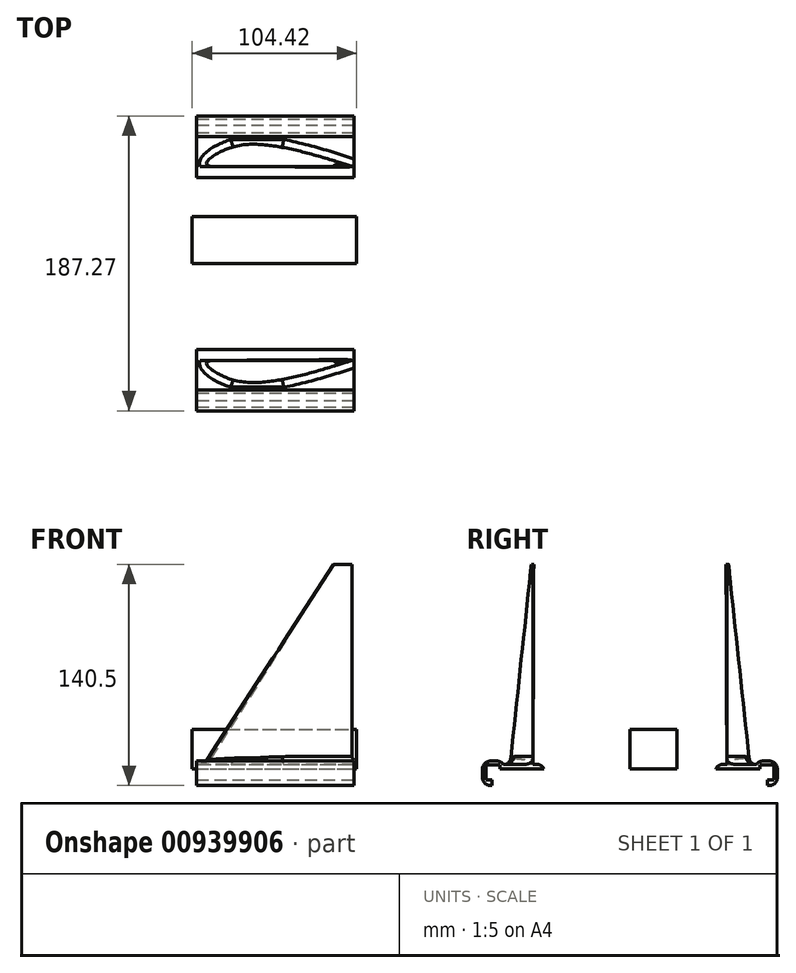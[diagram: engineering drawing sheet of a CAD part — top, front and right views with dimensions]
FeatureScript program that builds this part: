
annotation { "Feature Type Name" : "Feature", "Feature Type Description" : "" }
export const myFeature = defineFeature(function(context is Context, id is Id, definition is map)
    precondition{}
    {
        {
            var Q0;
            Q0=qCreatedBy(makeId("Top.planeOp"),FACE);
            var sketch = newSketch(context, id + "F0", { "sketchPlane" : qUnion([Q0])});
            skLineSegment(sketch, "E0", {"start": v(-39.77, 0) * mm, "end": v(53.98, 0) * mm});
            skFitSpline(sketch, "E1", {"points": [v(-39.77, 0) * mm, v(-32.14, 10.3) * mm, v(0, 14.02) * mm, v(53.98, 0) * mm], "startDerivative": vector(-78.5, 25.83) * mm, "endDerivative": vector(153.84, -50) * mm});
            skSolve(sketch);
        }
        {
            var Q0;
            Q0=qCreatedBy(makeId("Top.planeOp"),FACE);
            cPlane(context, id + "F1", {"entities" : qUnion([Q0]), "cplaneType" : CPlaneType.OFFSET, "offset" : 130 * mm, "width" : 150 * mm, "height" : 150 * mm});
        }
        {
            var Q0;
            Q0=qCreatedBy(id+"F1.planeOp",FACE);
            var sketch = newSketch(context, id + "F2", { "sketchPlane" : qUnion([Q0])});
            skFitSpline(sketch, "E2", {"points": [v(43.22, 0.93) * mm, v(45.42, 0.93) * mm, v(54, 0) * mm, v(42.54, 0) * mm, v(43.22, 0.93) * mm]});
            skLineSegment(sketch, "E3", {"start": v(42.54, 0) * mm, "end": v(54, 0) * mm});
            skSolve(sketch);
        }
        {
            var Q0;
            Q0 = qSketchRegion(id + "F2", true);
            var Q1;
            Q1 = qSketchRegion(id + "F0", true);
            loft(context, id + "F3", {"sheetProfilesArray" : [{ "sheetProfileEntities" : qUnion([Q0]) }, { "sheetProfileEntities" : qUnion([Q1]) }]});
        }
        {
            var Q0;
            Q0=makeQuery(id+"F0.imprint","IMPRINT",FACE,{"disambiguationData":[TD([[makeQuery(id+"F0.imprint","IMPRINT",EDGE,{"derivedFrom":sQuery(id+"F0.wireOp",EDGE,"E0")}),1.0]])]});
            var sketch = newSketch(context, id + "F4", { "sketchPlane" : qUnion([Q0])});
            skLineSegment(sketch, "E4.bottom", {"start": v(-44.66, -6.95) * mm, "end": v(55.34, -6.95) * mm});
            skLineSegment(sketch, "E4.top", {"start": v(-44.66, 17.05) * mm, "end": v(55.34, 17.05) * mm});
            skLineSegment(sketch, "E4.left", {"start": v(-44.66, -6.95) * mm, "end": v(-44.66, 17.05) * mm});
            skLineSegment(sketch, "E4.right", {"start": v(55.34, -6.95) * mm, "end": v(55.34, 17.05) * mm});
            skLineSegment(sketch, "E5", {"start": v(-44.66, 5.05) * mm, "end": v(55.34, 5.05) * mm, "construction": true});
            skLineSegment(sketch, "E6", {"start": v(5.34, -6.95) * mm, "end": v(5.34, 17.05) * mm, "construction": true});
            skSolve(sketch);
        }
        {
            var Q0;
            Q0 = qSketchRegion(id + "F4", true);
            extrude(context, id + "F5", {"entities" : qUnion([Q0]), "operationType" : NewBodyOperationType.ADD, "depth" : 3 * mm, "offsetDistance" : 25 * mm});
        }
        {
            var Q0;
            {var subQ0=sQuery(id+"F2.wireOp",EDGE,"E2");var subQ1=sQuery(id+"F2.wireOp",EDGE,"E3");var subQ2=sQuery(id+"F0.wireOp",EDGE,"E1");var subQ3=sQuery(id+"F0.wireOp",EDGE,"E0");Q0=makeQuery(id+"F5.boolean.opBoolean","INTERSECT",EDGE,{"derivedFrom":[makeQuery(id+"F3.opLoft","SWEPT_FACE",FACE,{"disambiguationData":[OSD([subQ3,subQ2,subQ0,subQ1]),TDD([makeQuery(id+"F0.imprint","INTERSECT",VERTEX,{"disambiguationData":[OD(0.0)],"derivedFrom":[subQ3,subQ2]}),makeQuery(id+"F0.imprint","INTERSECT",VERTEX,{"disambiguationData":[OD(1.0)],"derivedFrom":[subQ3,subQ2]}),makeQuery(id+"F0.imprint","IMPRINT",EDGE,{"derivedFrom":subQ2}),makeQuery(id+"F2.imprint","INTERSECT",VERTEX,{"disambiguationData":[OD(0.0)],"derivedFrom":[subQ0,subQ1]}),makeQuery(id+"F2.imprint","INTERSECT",VERTEX,{"disambiguationData":[OD(1.0)],"derivedFrom":[subQ0,subQ1]}),makeQuery(id+"F2.imprint","IMPRINT",EDGE,{"derivedFrom":subQ0})])]}),makeQuery(id+"F5.opExtrude","CAP_FACE",FACE,{"disambiguationData":[OSD([sQuery(id+"F4.wireOp",EDGE,"E4.bottom"),sQuery(id+"F4.wireOp",EDGE,"E4.top"),sQuery(id+"F4.wireOp",EDGE,"E4.left"),sQuery(id+"F4.wireOp",EDGE,"E4.right")])],"isStart":false})]});}
            fillet(context, id + "F6", {"entities" : qUnion([Q0]), "radius" : 5 * mm, "tangentPropagation" : true, "allowEdgeOverflow" : false});
        }
        {
            var Q0;
            Q0=makeQuery(id+"F5.opExtrude","SWEPT_FACE",FACE,{"disambiguationData":[OSD([sQuery(id+"F4.wireOp",EDGE,"E4.top")])]});
            extrude(context, id + "F7", {"entities" : qUnion([Q0]), "operationType" : NewBodyOperationType.ADD, "depth" : 4 * mm, "offsetDistance" : 25 * mm});
        }
        {
            var Q0;
            {var subQ0=sQuery(id+"F4.wireOp",EDGE,"E4.right");var subQ1=sQuery(id+"F4.wireOp",EDGE,"E4.left");var subQ2=sQuery(id+"F4.wireOp",EDGE,"E4.top");var subQ3=sQuery(id+"F4.wireOp",EDGE,"E4.bottom");var subQ4=makeQuery(id+"F5.opExtrude","CAP_FACE",FACE,{"disambiguationData":[OSD([subQ3,subQ2,subQ1,subQ0])],"isStart":false});Q0=makeQuery(id+"F7.boolean.opBoolean","MERGE",FACE,{"derivedFrom":[makeQuery(id+"F6.opFillet","SPLIT",FACE,{"disambiguationData":[OD(0.0)],"derivedFrom":subQ4}),makeQuery(id+"F6.opFillet","SPLIT",FACE,{"disambiguationData":[OD(1.0)],"derivedFrom":subQ4}),makeQuery(id+"F7.opExtrude","SWEPT_FACE",FACE,{"disambiguationData":[OSD([sQuery(id+"F0.wireOp",EDGE,"E0"),sQuery(id+"F0.wireOp",EDGE,"E1"),sQuery(id+"F2.wireOp",EDGE,"E2"),sQuery(id+"F2.wireOp",EDGE,"E3"),subQ3,subQ2,subQ1,subQ0])]})]});}
            var sketch = newSketch(context, id + "F8", { "sketchPlane" : qUnion([Q0])});
            skLineSegment(sketch, "E7.bottom", {"start": v(55.34, 21.05) * mm, "end": v(-44.66, 21.05) * mm});
            skLineSegment(sketch, "E7.top", {"start": v(55.34, 18.83) * mm, "end": v(-44.66, 18.83) * mm});
            skLineSegment(sketch, "E7.left", {"start": v(55.34, 21.05) * mm, "end": v(55.34, 18.83) * mm});
            skLineSegment(sketch, "E7.right", {"start": v(-44.66, 21.05) * mm, "end": v(-44.66, 18.83) * mm});
            skSolve(sketch);
        }
        {
            var Q0;
            Q0 = qSketchRegion(id + "F8", true);
            extrude(context, id + "F9", {"entities" : qUnion([Q0]), "operationType" : NewBodyOperationType.ADD, "depth" : 2 * mm, "offsetDistance" : 25 * mm});
        }
        {
            var Q0;
            Q0=makeQuery(id+"F9.boolean.opBoolean","MERGE",FACE,{"derivedFrom":[makeQuery(id+"F7.opExtrude","CAP_FACE",FACE,{"disambiguationData":[OSD([sQuery(id+"F4.wireOp",EDGE,"E4.top")])],"isStart":false}),makeQuery(id+"F9.opExtrude","SWEPT_FACE",FACE,{"disambiguationData":[OSD([sQuery(id+"F8.wireOp",EDGE,"E7.bottom")])]})]});
            var sketch = newSketch(context, id + "F10", { "sketchPlane" : qUnion([Q0])});
            skLineSegment(sketch, "E8.bottom", {"start": v(-55.34, 2.5) * mm, "end": v(44.66, 2.5) * mm});
            skLineSegment(sketch, "E8.top", {"start": v(-55.34, 5) * mm, "end": v(44.66, 5) * mm});
            skLineSegment(sketch, "E8.left", {"start": v(-55.34, 2.5) * mm, "end": v(-55.34, 5) * mm});
            skLineSegment(sketch, "E8.right", {"start": v(44.66, 2.5) * mm, "end": v(44.66, 5) * mm});
            skSolve(sketch);
        }
        {
            var Q0;
            Q0 = qSketchRegion(id + "F10", true);
            extrude(context, id + "F11", {"entities" : qUnion([Q0]), "operationType" : NewBodyOperationType.ADD, "depth" : 11 * mm, "offsetDistance" : 25 * mm});
        }
        {
            var Q0;
            Q0=makeQuery(id+"F11.opExtrude","SWEPT_FACE",FACE,{"disambiguationData":[OSD([sQuery(id+"F10.wireOp",EDGE,"E8.bottom")])]});
            var sketch = newSketch(context, id + "F12", { "sketchPlane" : qUnion([Q0])});
            skLineSegment(sketch, "E9.bottom", {"start": v(55.34, -32.05) * mm, "end": v(-44.66, -32.05) * mm});
            skLineSegment(sketch, "E9.top", {"start": v(55.34, -29.9) * mm, "end": v(-44.66, -29.9) * mm});
            skLineSegment(sketch, "E9.left", {"start": v(55.34, -32.05) * mm, "end": v(55.34, -29.9) * mm});
            skLineSegment(sketch, "E9.right", {"start": v(-44.66, -32.05) * mm, "end": v(-44.66, -29.9) * mm});
            skSolve(sketch);
        }
        {
            var Q0;
            Q0 = qSketchRegion(id + "F12", true);
            extrude(context, id + "F13", {"entities" : qUnion([Q0]), "operationType" : NewBodyOperationType.ADD, "depth" : 13 * mm, "offsetDistance" : 25 * mm});
        }
        {
            var Q0;
            Q0=makeQuery(id+"F11.opExtrude","CAP_EDGE",EDGE,{"disambiguationData":[OSD([sQuery(id+"F10.wireOp",EDGE,"E8.top")])],"isStart":false});
            var Q1;
            Q1=makeQuery(id+"F9.opExtrude","CAP_EDGE",EDGE,{"disambiguationData":[OSD([sQuery(id+"F8.wireOp",EDGE,"E7.top")])],"isStart":false});
            var Q2;
            Q2=makeQuery(id+"F5.opExtrude","CAP_EDGE",EDGE,{"disambiguationData":[OSD([sQuery(id+"F4.wireOp",EDGE,"E4.bottom")])],"isStart":false});
            fillet(context, id + "F14", {"entities" : qUnion([Q0, Q1, Q2]), "radius" : 5 * mm, "tangentPropagation" : true, "allowEdgeOverflow" : false});
        }
        {
            var Q0;
            Q0=makeQuery(id+"F13.opExtrude","SWEPT_FACE",FACE,{"disambiguationData":[OSD([sQuery(id+"F12.wireOp",EDGE,"E9.top")])]});
            var sketch = newSketch(context, id + "F15", { "sketchPlane" : qUnion([Q0])});
            skLineSegment(sketch, "E10.bottom", {"start": v(-44.66, -10.5) * mm, "end": v(55.34, -10.5) * mm});
            skLineSegment(sketch, "E10.top", {"start": v(-44.66, -7.07) * mm, "end": v(55.34, -7.07) * mm});
            skLineSegment(sketch, "E10.left", {"start": v(-44.66, -10.5) * mm, "end": v(-44.66, -7.07) * mm});
            skLineSegment(sketch, "E10.right", {"start": v(55.34, -10.5) * mm, "end": v(55.34, -7.07) * mm});
            skSolve(sketch);
        }
        {
            var Q0;
            Q0 = qSketchRegion(id + "F15", true);
            extrude(context, id + "F16", {"entities" : qUnion([Q0]), "operationType" : NewBodyOperationType.ADD, "depth" : 4 * mm, "offsetDistance" : 25 * mm});
        }
        {
            var Q0;
            Q0=makeQuery(id+"F13.opExtrude","CAP_EDGE",EDGE,{"disambiguationData":[OSD([sQuery(id+"F12.wireOp",EDGE,"E9.bottom")])],"isStart":false});
            fillet(context, id + "F17", {"entities" : qUnion([Q0]), "radius" : 5 * mm, "tangentPropagation" : true, "allowEdgeOverflow" : false});
        }
        {
            var Q0;
            Q0=qCreatedBy(makeId("Top.planeOp"),FACE);
            var sketch = newSketch(context, id + "F18", { "sketchPlane" : qUnion([Q0])});
            skLineSegment(sketch, "E11.bottom", {"start": v(-47.46, -31.79) * mm, "end": v(56.96, -31.79) * mm});
            skLineSegment(sketch, "E11.top", {"start": v(-47.46, -61.58) * mm, "end": v(56.96, -61.58) * mm});
            skLineSegment(sketch, "E11.left", {"start": v(-47.46, -31.79) * mm, "end": v(-47.46, -61.58) * mm});
            skLineSegment(sketch, "E11.right", {"start": v(56.96, -31.79) * mm, "end": v(56.96, -61.58) * mm});
            skSolve(sketch);
        }
        {
            var Q0;
            Q0 = qSketchRegion(id + "F18", true);
            extrude(context, id + "F19", {"entities" : qUnion([Q0]), "depth" : 25 * mm, "offsetDistance" : 25 * mm});
        }
        {
            var Q0;
            Q0=makeQuery(id+"F3.opLoft","SWEPT_BODY",BODY,{"disambiguationData":[OSD([makeQuery(id+"F0.imprint","IMPRINT",FACE,{"disambiguationData":[TD([[makeQuery(id+"F0.imprint","IMPRINT",EDGE,{"derivedFrom":sQuery(id+"F0.wireOp",EDGE,"E0")}),1.0]])]}),makeQuery(id+"F2.imprint","IMPRINT",FACE,{"disambiguationData":[TD([[makeQuery(id+"F2.imprint","IMPRINT",EDGE,{"derivedFrom":sQuery(id+"F2.wireOp",EDGE,"E2")}),-1.0]])]})])]});
            var Q1;
            Q1=makeQuery(id+"F19.opExtrude","SWEPT_FACE",FACE,{"disambiguationData":[OSD([sQuery(id+"F18.wireOp",EDGE,"E11.top")])]});
            mirror(context, id + "F20", {"operationType" : NewBodyOperationType.ADD, "entities" : qUnion([Q0]), "mirrorPlane" : qUnion([Q1])});
        }
    });
